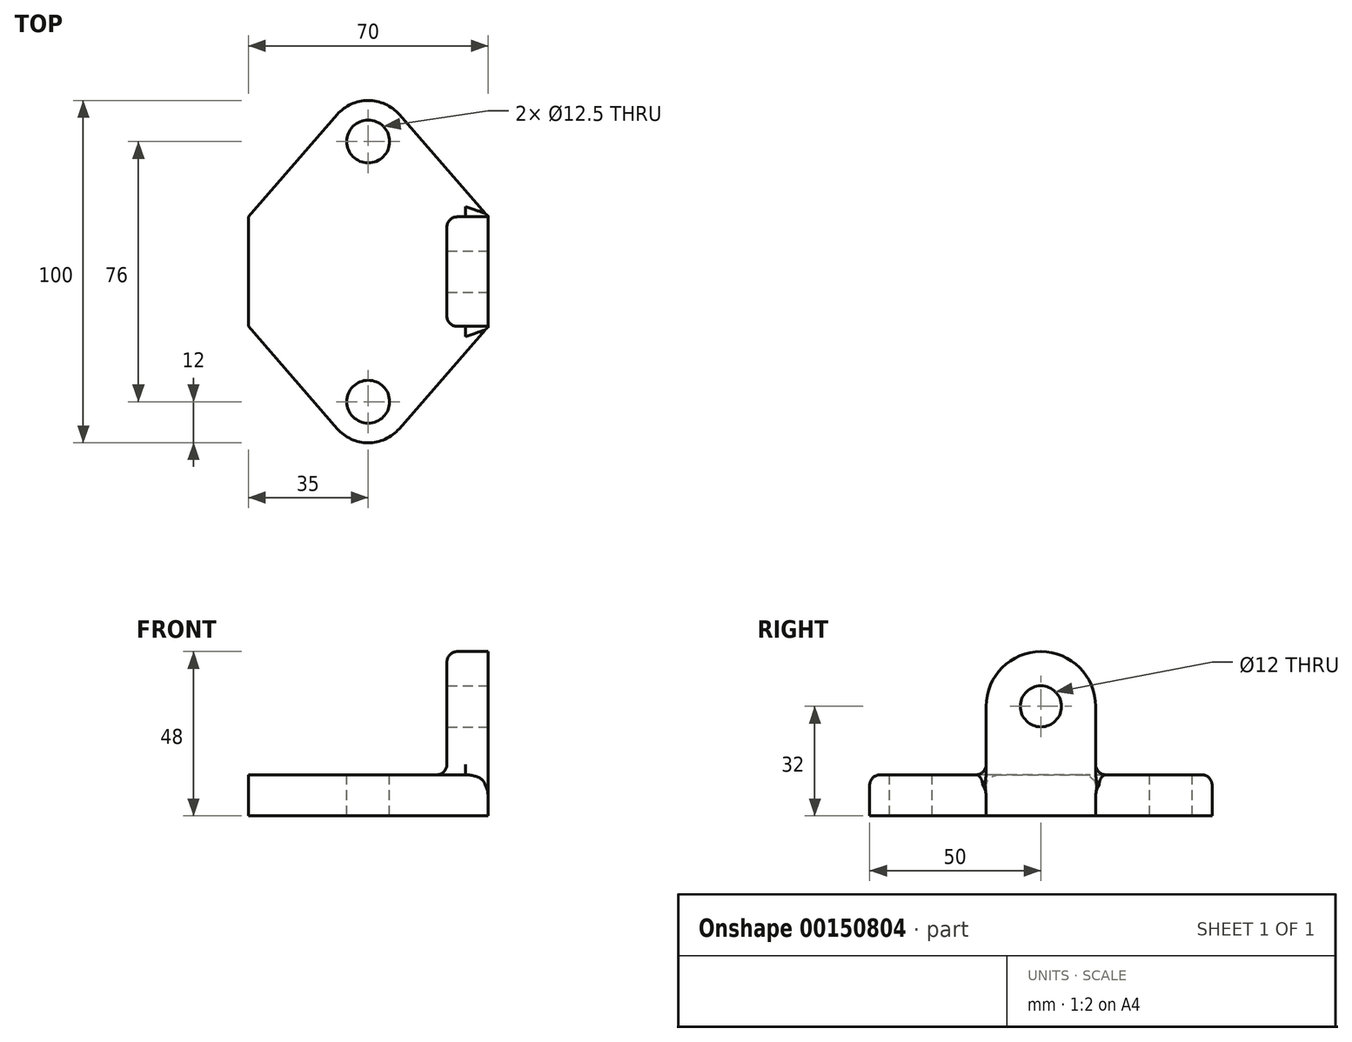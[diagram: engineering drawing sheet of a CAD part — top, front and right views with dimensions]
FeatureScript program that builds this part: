
annotation { "Feature Type Name" : "Feature", "Feature Type Description" : "" }
export const myFeature = defineFeature(function(context is Context, id is Id, definition is map)
    precondition{}
    {
        {
            var Q0;
            Q0=qCreatedBy(makeId("Top.planeOp"),FACE);
            var sketch = newSketch(context, id + "F0", { "sketchPlane" : qUnion([Q0])});
            skLineSegment(sketch, "E0", {"start": v(0, 62.74) * mm, "end": v(0, -56.64) * mm, "construction": true});
            skLineSegment(sketch, "E1.bottom", {"start": v(-35, 0) * mm, "end": v(35, 0) * mm});
            skLineSegment(sketch, "E1.left", {"start": v(-35, 0) * mm, "end": v(-35, -16) * mm});
            skLineSegment(sketch, "E1.right", {"start": v(35, 0) * mm, "end": v(35, -16) * mm});
            skLineSegment(sketch, "E2", {"start": v(-35, -16) * mm, "end": v(-9.06, -45.87) * mm});
            skLineSegment(sketch, "E3", {"start": v(-9.06, -45.87) * mm, "end": v(9.06, -45.87) * mm});
            skLineSegment(sketch, "E4", {"start": v(9.06, -45.87) * mm, "end": v(35, -16) * mm});
            skArc(sketch, "E5", {"start": v(-9.06, -45.87) * mm, "mid": v(0, -50) * mm, "end": v(9.06, -45.87) * mm});
            skCircle(sketch, "E6", {"center": v(0, -38) * mm, "radius": 6.25 * mm});
            skSolve(sketch);
        }
        {
            var Q0;
            Q0=makeQuery(id+"F0.imprint","IMPRINT",FACE,{"disambiguationData":[TD([[makeQuery(id+"F0.imprint","IMPRINT",EDGE,{"derivedFrom":sQuery(id+"F0.wireOp",EDGE,"E1.bottom")}),-1.0]])]});
            var Q1;
            Q1=makeQuery(id+"F0.imprint","IMPRINT",FACE,{"disambiguationData":[TD([[makeQuery(id+"F0.imprint","IMPRINT",EDGE,{"derivedFrom":sQuery(id+"F0.wireOp",EDGE,"E3")}),-1.0]])]});
            var Q2;
            Q2=makeQuery(id+"F0.imprint","IMPRINT",FACE,{"disambiguationData":[TD([[makeQuery(id+"F0.imprint","IMPRINT",EDGE,{"derivedFrom":sQuery(id+"F0.wireOp",EDGE,"E6")}),1.0]])]});
            extrude(context, id + "F1", {"entities" : qUnion([Q0, Q1, Q2]), "depth" : 12 * mm});
        }
        {
            var Q0;
            Q0=makeQuery(id+"F1.opExtrude","SWEPT_BODY",BODY,{"disambiguationData":[OSD([sQuery(id+"F0.wireOp",EDGE,"E1.bottom"),sQuery(id+"F0.wireOp",EDGE,"E1.left"),sQuery(id+"F0.wireOp",EDGE,"E1.right"),sQuery(id+"F0.wireOp",EDGE,"E2"),sQuery(id+"F0.wireOp",EDGE,"E4"),sQuery(id+"F0.wireOp",EDGE,"E5")])]});
            var Q1;
            Q1=qCreatedBy(makeId("Front.planeOp"),FACE);
            mirror(context, id + "F2", {"operationType" : NewBodyOperationType.ADD, "entities" : qUnion([Q0]), "mirrorPlane" : qUnion([Q1])});
        }
        {
            var Q0;
            {var subQ0=makeQuery(id+"F1.opExtrude","SWEPT_FACE",FACE,{"disambiguationData":[OSD([sQuery(id+"F0.wireOp",EDGE,"E1.right")])]});Q0=makeQuery(id+"F2.boolean.opBoolean","MERGE",FACE,{"derivedFrom":[subQ0,makeQuery(id+"F2.opPattern","COPY",FACE,{"derivedFrom":subQ0,"instanceName":"1"})]});}
            var sketch = newSketch(context, id + "F3", { "sketchPlane" : qUnion([Q0])});
            skLineSegment(sketch, "E7.bottom", {"start": v(-16, 0) * mm, "end": v(16, 0) * mm});
            skLineSegment(sketch, "E7.top", {"start": v(-16, 32) * mm, "end": v(16, 32) * mm});
            skLineSegment(sketch, "E7.left", {"start": v(-16, 0) * mm, "end": v(-16, 32) * mm});
            skLineSegment(sketch, "E7.right", {"start": v(16, 0) * mm, "end": v(16, 32) * mm});
            skArc(sketch, "E8", {"start": v(16, 32) * mm, "mid": v(0, 48) * mm, "end": v(-16, 32) * mm});
            skSolve(sketch);
        }
        {
            var Q0;
            Q0=makeQuery(id+"F3.imprint","IMPRINT",FACE,{"disambiguationData":[TD([[makeQuery(id+"F3.imprint","IMPRINT",EDGE,{"derivedFrom":sQuery(id+"F3.wireOp",EDGE,"E7.top")}),1.0]])]});
            var Q1;
            {var subQ0=sQuery(id+"F3.wireOp",EDGE,"E7.top");Q1=makeQuery(id+"F3.imprint","IMPRINT",FACE,{"disambiguationData":[TD([[makeQuery(id+"F3.imprint","IMPRINT",EDGE,{"derivedFrom":subQ0}),-1.0]])]});}
            var Q2;
            {var subQ0=sQuery(id+"F3.wireOp",EDGE,"E7.bottom");Q2=makeQuery(id+"F3.imprint","IMPRINT",FACE,{"disambiguationData":[TD([[makeQuery(id+"F3.imprint","IMPRINT",EDGE,{"derivedFrom":subQ0}),-1.0]])]});}
            extrude(context, id + "F4", {"entities" : qUnion([Q0, Q1, Q2]), "operationType" : NewBodyOperationType.ADD, "oppositeDirection" : true, "depth" : 12 * mm});
        }
        {
            var Q0;
            {var subQ0=makeQuery(id+"F1.opExtrude","CAP_FACE",FACE,{"disambiguationData":[OSD([sQuery(id+"F0.wireOp",EDGE,"E1.bottom"),sQuery(id+"F0.wireOp",EDGE,"E1.left"),sQuery(id+"F0.wireOp",EDGE,"E1.right"),sQuery(id+"F0.wireOp",EDGE,"E2"),sQuery(id+"F0.wireOp",EDGE,"E4"),sQuery(id+"F0.wireOp",EDGE,"E5")])],"isStart":false});Q0=makeQuery(id+"F2.boolean.opBoolean","MERGE",FACE,{"derivedFrom":[subQ0,makeQuery(id+"F2.opPattern","COPY",FACE,{"derivedFrom":subQ0,"instanceName":"1"})]});}
            var sketch = newSketch(context, id + "F5", { "sketchPlane" : qUnion([Q0])});
            skCircle(sketch, "E9.0", {"center": v(0, -38) * mm, "radius": 6.25 * mm});
            skSolve(sketch);
        }
        {
            var Q0;
            Q0=makeQuery(id+"F5.imprint","IMPRINT",FACE,{"disambiguationData":[TD([[makeQuery(id+"F5.imprint","IMPRINT",EDGE,{"derivedFrom":sQuery(id+"F5.wireOp",EDGE,"E9.0")}),-1.0]])]});
            var sketch = newSketch(context, id + "F6", { "sketchPlane" : qUnion([Q0])});
            skCircle(sketch, "E10.0", {"center": v(0, 38) * mm, "radius": 6.25 * mm});
            skSolve(sketch);
        }
        {
            var Q0;
            Q0=qSketchRegion(id+"F6",true);
            var Q1;
            Q1=qSketchRegion(id+"F5",true);
            extrude(context, id + "F7", {"entities" : qUnion([Q0, Q1]), "operationType" : NewBodyOperationType.REMOVE, "endBound" : BoundingType.THROUGH_ALL, "oppositeDirection" : true, "depth" : 25 * mm});
        }
        {
            var Q0;
            {var subQ0=makeQuery(id+"F1.opExtrude","SWEPT_FACE",FACE,{"disambiguationData":[OSD([sQuery(id+"F0.wireOp",EDGE,"E1.right")])]});Q0=makeQuery(id+"F4.boolean.opBoolean","MERGE",FACE,{"derivedFrom":[makeQuery(id+"F2.boolean.opBoolean","MERGE",FACE,{"derivedFrom":[subQ0,makeQuery(id+"F2.opPattern","COPY",FACE,{"derivedFrom":subQ0,"instanceName":"1"})]}),makeQuery(id+"F4.opExtrude","CAP_FACE",FACE,{"disambiguationData":[OSD([sQuery(id+"F3.wireOp",EDGE,"E7.bottom"),sQuery(id+"F3.wireOp",EDGE,"E7.left"),sQuery(id+"F3.wireOp",EDGE,"E7.right"),sQuery(id+"F3.wireOp",EDGE,"E8")])],"isStart":true})]});}
            var sketch = newSketch(context, id + "F8", { "sketchPlane" : qUnion([Q0])});
            skCircle(sketch, "E11", {"center": v(0, 32) * mm, "radius": 6 * mm});
            skSolve(sketch);
        }
        {
            var Q0;
            Q0=qSketchRegion(id+"F8",true);
            extrude(context, id + "F9", {"entities" : qUnion([Q0]), "operationType" : NewBodyOperationType.REMOVE, "endBound" : BoundingType.THROUGH_ALL, "oppositeDirection" : true, "depth" : 25 * mm});
        }
        {
            var Q0;
            Q0=makeQuery(id+"F2.opPattern","COPY",EDGE,{"derivedFrom":makeQuery(id+"F1.opExtrude","CAP_EDGE",EDGE,{"disambiguationData":[OSD([sQuery(id+"F0.wireOp",EDGE,"E2")])],"isStart":false}),"instanceName":"1"});
            var Q1;
            Q1=makeQuery(id+"F1.opExtrude","CAP_EDGE",EDGE,{"disambiguationData":[OSD([sQuery(id+"F0.wireOp",EDGE,"E4")])],"isStart":false});
            var Q2;
            Q2=makeQuery(id+"FWKPYHZQDnc0K3y_1.1.F2.opPattern","COPY",EDGE,{"derivedFrom":makeQuery(id+"F4.opExtrude","CAP_EDGE",EDGE,{"disambiguationData":[OSD([sQuery(id+"F3.wireOp",EDGE,"E8")])],"isStart":false}),"instanceName":"1"});
            var Q3;
            Q3=makeQuery(id+"F4.opExtrude","CAP_EDGE",EDGE,{"disambiguationData":[OSD([sQuery(id+"F3.wireOp",EDGE,"E8")])],"isStart":false});
            fillet(context, id + "F10", {"entities" : qUnion([Q0, Q1, Q2, Q3]), "radius" : 3 * mm, "tangentPropagation" : true, "allowEdgeOverflow" : false});
        }
        {
            var Q0;
            {var subQ0=makeQuery(id+"F1.opExtrude","CAP_FACE",FACE,{"disambiguationData":[OSD([sQuery(id+"F0.wireOp",EDGE,"E1.bottom"),sQuery(id+"F0.wireOp",EDGE,"E1.left"),sQuery(id+"F0.wireOp",EDGE,"E1.right"),sQuery(id+"F0.wireOp",EDGE,"E2"),sQuery(id+"F0.wireOp",EDGE,"E4"),sQuery(id+"F0.wireOp",EDGE,"E5")])],"isStart":false});Q0=makeQuery(id+"FWKPYHZQDnc0K3y_1.1.F2.opPattern","COPY",EDGE,{"derivedFrom":makeQuery(id+"F4.boolean.opBoolean","INTERSECT",EDGE,{"derivedFrom":[makeQuery(id+"F2.boolean.opBoolean","MERGE",FACE,{"derivedFrom":[subQ0,makeQuery(id+"F2.opPattern","COPY",FACE,{"derivedFrom":subQ0,"instanceName":"1"})]}),makeQuery(id+"F4.opExtrude","CAP_FACE",FACE,{"disambiguationData":[OSD([sQuery(id+"F3.wireOp",EDGE,"E7.bottom"),sQuery(id+"F3.wireOp",EDGE,"E7.left"),sQuery(id+"F3.wireOp",EDGE,"E7.right"),sQuery(id+"F3.wireOp",EDGE,"E8")])],"isStart":false})]}),"instanceName":"1"});}
            var Q1;
            {var subQ0=makeQuery(id+"F1.opExtrude","CAP_FACE",FACE,{"disambiguationData":[OSD([sQuery(id+"F0.wireOp",EDGE,"E1.bottom"),sQuery(id+"F0.wireOp",EDGE,"E1.left"),sQuery(id+"F0.wireOp",EDGE,"E1.right"),sQuery(id+"F0.wireOp",EDGE,"E2"),sQuery(id+"F0.wireOp",EDGE,"E4"),sQuery(id+"F0.wireOp",EDGE,"E5")])],"isStart":false});Q1=makeQuery(id+"F4.boolean.opBoolean","INTERSECT",EDGE,{"derivedFrom":[makeQuery(id+"F2.boolean.opBoolean","MERGE",FACE,{"derivedFrom":[subQ0,makeQuery(id+"F2.opPattern","COPY",FACE,{"derivedFrom":subQ0,"instanceName":"1"})]}),makeQuery(id+"F4.opExtrude","SWEPT_FACE",FACE,{"disambiguationData":[OSD([sQuery(id+"F3.wireOp",EDGE,"E7.left")])]})]});}
            fillet(context, id + "F11", {"entities" : qUnion([Q0, Q1]), "radius" : 3 * mm, "tangentPropagation" : true, "allowEdgeOverflow" : false});
        }
    });
